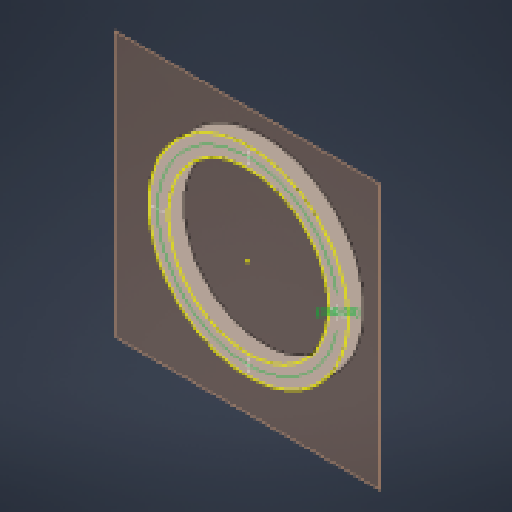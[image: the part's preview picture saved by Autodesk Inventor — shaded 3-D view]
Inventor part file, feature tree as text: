
AUTODESK INVENTOR PART (.ipt)
format: ipt  version: 2024 (Build 280153000, 153)  size: 145,920 bytes
history: native  units: in
note: dims shown in document units (in); Inventor stores cm internally (conversion verified against a paired STEP export)
features: plane x2, sketch x2, other x2, extrude x1, hole x1, reference x1
ambient origin geometry x8: Origin, YZ Plane, XZ Plane, XY Plane, X Axis, Y Axis, Z Axis, Center Point
bodies: Solid1 (feature_tree)
feature tree (9):
  plane  "Work Plane1"
  sketch  "Sketch1"  dims[d0=3.8976in d1=0.4724in]
  plane  "Work Plane2"
  extrude  "Extrusion1"  Depth=0.4724in
  hole  "Hole1"  [1 undecoded]
  reference  "Reference1"
  sketch  "Sketch2"  dims[d2=1.5748in d4=360.0deg d6=1.0in d7=0.0in d8=1.5748in d10=360.0deg d12=0.1969in d13=0.75in d14=0.409in d15=0.25in d16=90.0deg d17=1.0in d18=0.8108in]
  other  "Assembly1"
  other  "OR:1"
note: 1 required parameter value undecoded (feature->parameter linkage not recoverable at this tier; creation-order binding heuristic only, values carry confidence <= 0.55)
